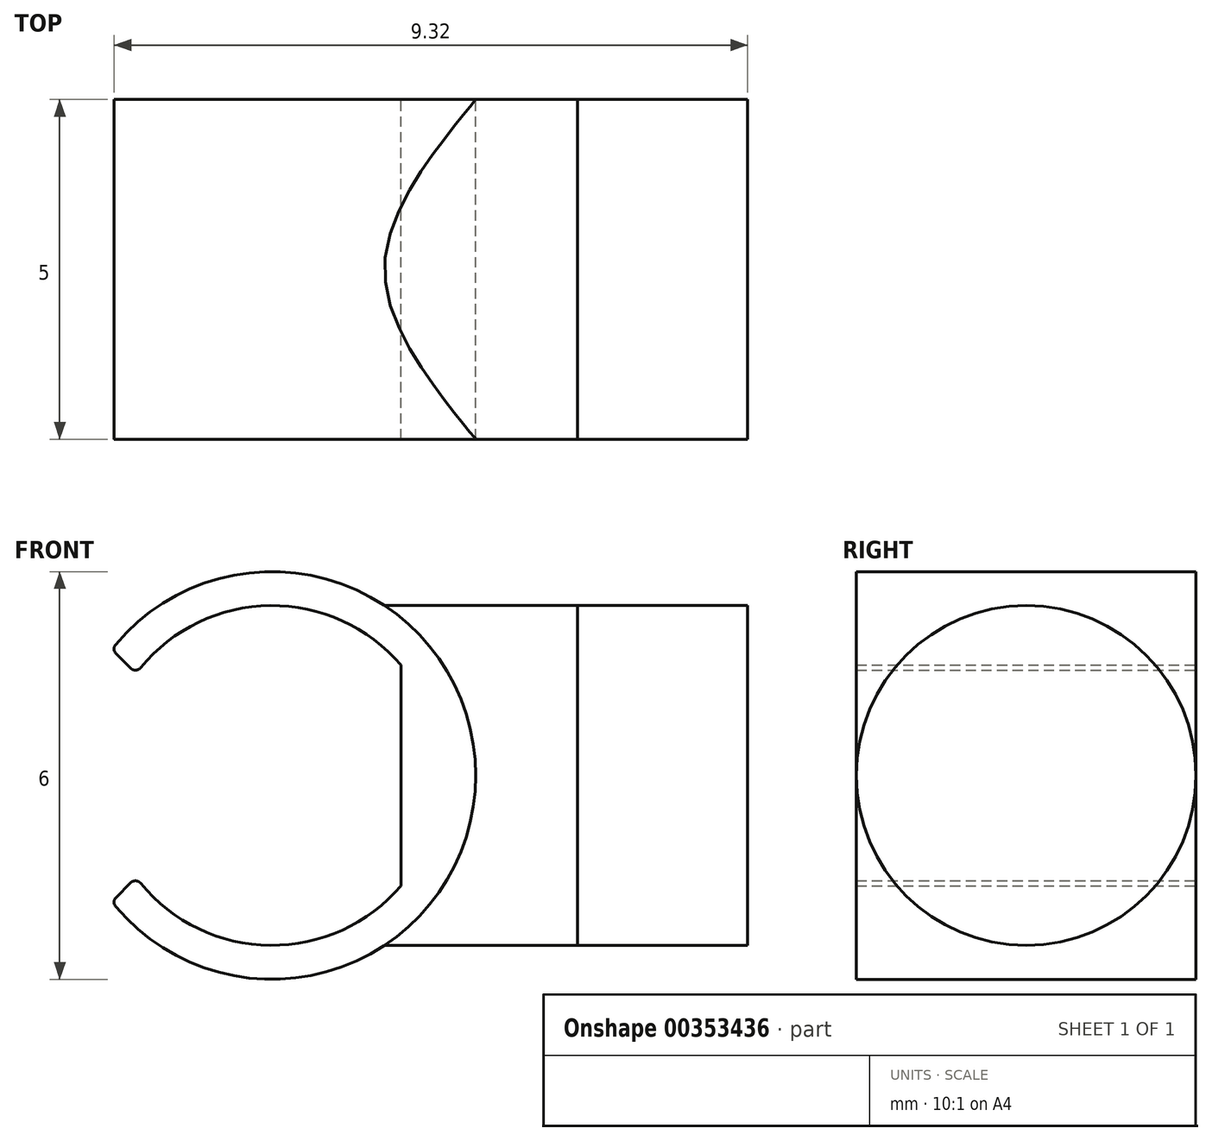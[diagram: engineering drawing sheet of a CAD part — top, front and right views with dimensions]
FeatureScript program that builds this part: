
annotation { "Feature Type Name" : "Feature", "Feature Type Description" : "" }
export const myFeature = defineFeature(function(context is Context, id is Id, definition is map)
    precondition{}
    {
        {
            var Q0;
            Q0=qCreatedBy(makeId("Right.planeOp"),FACE);
            var sketch = newSketch(context, id + "F0", { "sketchPlane" : qUnion([Q0])});
            skCircle(sketch, "E0", {"center": v(0, 0) * mm, "radius": 2.5 * mm});
            skSolve(sketch);
        }
        {
            var Q0;
            Q0=makeQuery(id+"F0.imprint","IMPRINT",FACE,{"disambiguationData":[TD([[makeQuery(id+"F0.imprint","IMPRINT",EDGE,{"derivedFrom":sQuery(id+"F0.wireOp",EDGE,"E0")}),1.0]])]});
            extrude(context, id + "F1", {"entities" : qUnion([Q0]), "endBound" : BoundingType.SYMMETRIC, "depth" : 2.5 * mm});
        }
        {
            var Q0;
            Q0=qCreatedBy(makeId("Front.planeOp"),FACE);
            var sketch = newSketch(context, id + "F2", { "sketchPlane" : qUnion([Q0])});
            skArc(sketch, "E1", {"start": v(-7.68, -1.59) * mm, "mid": v(-5.77, -2.5) * mm, "end": v(-3.85, -1.62) * mm});
            skArc(sketch, "E2", {"start": v(-8.05, 1.93) * mm, "mid": v(-2.75, 0) * mm, "end": v(-8.05, -1.93) * mm});
            skLineSegment(sketch, "E3", {"start": v(-7.83, 1.58) * mm, "end": v(-8.04, 1.8) * mm});
            skLineSegment(sketch, "E4", {"start": v(-7.83, -1.58) * mm, "end": v(-8.04, -1.8) * mm});
            skPoint(sketch, "E5.visualSharp", {"position": v(-8.1, 1.86) * mm});
            skArc(sketch, "E5.filletArc", {"start": v(-8.05, 1.93) * mm, "mid": v(-8.07, 1.86) * mm, "end": v(-8.04, 1.8) * mm});
            skPoint(sketch, "E6.visualSharp", {"position": v(-7.75, 1.5) * mm});
            skArc(sketch, "E6.filletArc", {"start": v(-7.83, 1.58) * mm, "mid": v(-7.75, 1.55) * mm, "end": v(-7.68, 1.59) * mm});
            skPoint(sketch, "E7.visualSharp", {"position": v(-8.1, -1.86) * mm});
            skArc(sketch, "E7.filletArc", {"start": v(-8.04, -1.8) * mm, "mid": v(-8.07, -1.86) * mm, "end": v(-8.05, -1.93) * mm});
            skPoint(sketch, "E8.visualSharp", {"position": v(-7.75, -1.5) * mm});
            skArc(sketch, "E8.filletArc", {"start": v(-7.68, -1.59) * mm, "mid": v(-7.75, -1.55) * mm, "end": v(-7.83, -1.58) * mm});
            skLineSegment(sketch, "E9", {"start": v(-3.85, 1.62) * mm, "end": v(-3.85, -1.62) * mm});
            skArc(sketch, "E10.trimOffspring", {"start": v(-3.85, 1.62) * mm, "mid": v(-5.77, 2.5) * mm, "end": v(-7.68, 1.59) * mm});
            skSolve(sketch);
        }
        {
            var Q0;
            Q0=makeQuery(id+"F2.imprint","IMPRINT",FACE,{"disambiguationData":[TD([[makeQuery(id+"F2.imprint","IMPRINT",EDGE,{"derivedFrom":sQuery(id+"F2.wireOp",EDGE,"E1")}),-1.0]])]});
            extrude(context, id + "F3", {"entities" : qUnion([Q0]), "endBound" : BoundingType.SYMMETRIC, "depth" : 5 * mm});
        }
        {
            var Q0;
            Q0=makeQuery(id+"F1.opExtrude","CAP_FACE",FACE,{"disambiguationData":[OSD([sQuery(id+"F0.wireOp",EDGE,"E0")])],"isStart":true});
            var Q1;
            Q1=makeQuery(id+"F3.opExtrude","SWEPT_BODY",BODY,{"disambiguationData":[OSD([sQuery(id+"F2.wireOp",EDGE,"E1"),sQuery(id+"F2.wireOp",EDGE,"E2"),sQuery(id+"F2.wireOp",EDGE,"E3"),sQuery(id+"F2.wireOp",EDGE,"E4"),sQuery(id+"F2.wireOp",EDGE,"E5.filletArc"),sQuery(id+"F2.wireOp",EDGE,"E6.filletArc"),sQuery(id+"F2.wireOp",EDGE,"E7.filletArc"),sQuery(id+"F2.wireOp",EDGE,"E8.filletArc"),sQuery(id+"F2.wireOp",EDGE,"E9"),sQuery(id+"F2.wireOp",EDGE,"E10.trimOffspring")])]});
            extrude(context, id + "F4", {"entities" : qUnion([Q0]), "endBound" : BoundingType.UP_TO_BODY, "endBoundEntityBody" : qUnion([Q1]), "depth" : 25 * mm});
        }
    });
